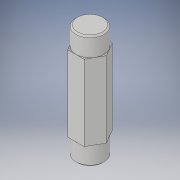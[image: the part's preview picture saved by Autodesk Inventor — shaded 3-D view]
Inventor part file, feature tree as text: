
AUTODESK INVENTOR PART (.ipt)
format: ipt  version: 2018 (Build 220112000, 112)  size: 108,544 bytes
history: native  units: in
note: dims shown in document units (in); Inventor stores cm internally (conversion verified against a paired STEP export)
features: chamfer x1
ambient origin geometry x8: Origin, YZ Plane, XZ Plane, XY Plane, X Axis, Y Axis, Z Axis, Center Point
bodies: Solid1 (feature_tree)
feature tree (1):
  chamfer  "Chamfer2"  [1 undecoded]
note: 1 required parameter value undecoded (feature->parameter linkage not recoverable at this tier; creation-order binding heuristic only, values carry confidence <= 0.55)
